# Revit family: Sichtrohrschelle, TPE weiß
name_source: partatom
category: HLS-Bauteile
revit_build: Autodesk Revit 2017 (Build: 20190507_1515(x64)
units: mm (PartAtom-declared; Revit-internal decimal feet)

## family parameters
Arbeitsebenenbasiert = Ja
Beim Laden mit Abzugskörper schneiden = Nein
Bemaßung runder Anschluss = Durchmesser verwenden
Gemeinsam genutzt = Ja
Immer vertikal = Nein
Raumberechnungspunkt = Nein
Teiletyp = Normal

## types (3) — shared parameters
Anschluss = Lasche für M6
Bauart = einteilig
DS = 5 mm  [stored 0.0164042 ft]
DVS = 7 mm  [stored 0.0229659 ft]
Dämmstärke = 5 mm  [stored 0.0164042 ft]
Fabrikat = MEFA
Farbe Schalldämmeinlage = weiß
Gewicht = 0.04 kg
Gewicht pro Bauteil = 0.04 kg
Kurztext1 = Sichtrohrschelle Duplo 20x1,0
MB = 20 mm  [stored 0.0656168 ft]
MD = 1 mm  [stored 0.00328084 ft]
Material = Stahl
Material Schalldämmeinlage = TPE
Materialmaße = 20x1,0 mm
Materialname = DC01-A, DD11
Mengeneinheit = St
Oberflaeche = galvanisch verzinkt
Schalldämmeinlage = Gummi
Verschluss = Schraubverschluss
Verschluss-Schraube = M6
Vorgabe-Ansicht = 1219 mm
max. Temperaturbeständigkeit = 100 °C
max. zul. Last = 0.65 kN
max. zul. Last horizontal = 0.00 kN
max. zul. Last vertikal = 0.00 kN
vpe = 100 St
zero-valued in all types: Nennweite DN Rohr, Stärke Material, max. Rohraußendurchmesser, min. Rohraußendurchmesser

## per-type parameters (varying)
| type | A | Anschlußhöhe | Artikelnummer | B | Breite | D | D0 | EAN | H | Höhe | Kurztext2 | L | R | RM | Rohraußendurchmesser | Rohraußendurchmesser Zoll | max. Höhe |
| Sichtrohrschelle, Ø15 mm, TPE weiß | 33 mm | 33 mm | 0311150 | 27 mm | 31 mm | 15 mm  [stored 0.0492126 ft] | 25 mm  [stored 0.082021 ft] | 4250928407634 | 54 mm | 56 mm | 15 mm TPE | 41 mm | 8 mm  [stored 0.0262467 ft] | 14 mm  [stored 0.0459318 ft] | 15 mm  [stored 0.0492126 ft] | Zoll | 56 mm |
| Sichtrohrschelle, Ø18 mm, TPE weiß | 31 mm | 31 mm | 0311180 | 30 mm | 34 mm | 18 mm  [stored 0.0590551 ft] | 28 mm  [stored 0.0918635 ft] | 4250928407641 | 55 mm  [stored 0.180446 ft] | 57 mm | 18 mm TPE | 40 mm  [stored 0.131234 ft] | 9 mm  [stored 0.0295276 ft] | 15 mm  [stored 0.0492126 ft] | 18 mm  [stored 0.0590551 ft] | 3/8 Zoll | 57 mm |
| Sichtrohrschelle, Ø22 mm, TPE weiß | 31 mm | 31 mm | 0311220 | 34 mm | 38 mm | 22 mm | 32 mm  [stored 0.104987 ft] | 4250928407658 | 59 mm | 61 mm | 22 mm TPE | 42 mm | 11 mm | 17 mm | 22 mm | 1/2 Zoll | 61 mm |

note: [stored X ft] marks values corroborated as IEEE doubles in the binary element streams (Revit-internal decimal feet)

## geometry (parser evidence)
native form markers: Sweep x5
no freeform markers — native parametric forms only
